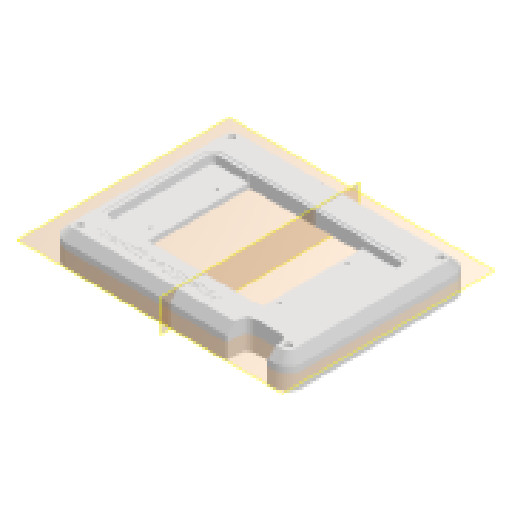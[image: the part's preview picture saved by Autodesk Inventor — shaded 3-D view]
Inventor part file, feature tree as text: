
AUTODESK INVENTOR PART (.ipt)
format: ipt  version: 2024.1 (Build 281209000, 209)  size: 909,824 bytes
history: native  units: mm
features: sketch x9, extrude x8, reference x8, projected_geometry x8, plane x5, other x4, chamfer x1, hole x1
ambient origin geometry x8: Origin, YZ Plane, XZ Plane, XY Plane, X Axis, Y Axis, Z Axis, Center Point
bodies: Volumenkörper1 (feature_tree)
feature tree (44):
  plane  "Arbeitsebene1"
  plane  "Arbeitsebene2"
  extrude  "Extrusion1"  Depth=10.0mm
  plane  "Arbeitsebene3"
  extrude  "Extrusion2"  Depth=10.0mm TaperAngle=0.0deg
  sketch  "Skizze3"  dims[d10=10.0mm d11=0.0mm d12=8.0mm d13=2.0mm d14=45.0deg]
  plane  "Arbeitsebene4"
  extrude  "Extrusion3"  Depth=8.0mm TaperAngle=45.0deg
  chamfer  "Fasen1"  [1 undecoded]
  extrude  "Extrusion4"  Depth=15.0mm TaperAngle=0.0deg
  extrude  "Extrusion5"  Depth=14.0mm
  extrude  "Extrusion6"  Depth=14.0mm
  hole  "Bohrung1"  [1 undecoded]
  extrude  "Extrusion7"  Depth=14.0mm
  extrude  "Extrusion8"  Depth=14.0mm
  plane  "Arbeitsebene5"
  sketch  "Skizze1"  dims[d2=1.0mm d3=0.0mm d4=10.0mm]
  reference  "Referenz2"
  reference  "Referenz3"
  reference  "Referenz4"
  reference  "Referenz5"
  reference  "Referenz6"
  sketch  "Skizze2"  dims[d5=5.0mm d7=10.0mm d8=0.0mm]
  sketch  "Skizze4"  dims[d15=40.0mm]
  reference  "Referenz9"
  projected_geometry  "Projizierte Kontur3"
  sketch  "Skizze5"  dims[d16=20.0mm]
  projected_geometry  "Projizierte Kontur4"
  sketch  "Skizze6"  dims[d17=7.0mm]
  projected_geometry  "Projizierte Kontur5"
  sketch  "Skizze7"  dims[d18=20.0mm d19=0.0mm d20=0.0mm]
  reference  "Referenz10"
  projected_geometry  "Projizierte Kontur6"
  sketch  "Skizze8"  dims[d21=6.0mm d22=15.0mm d23=0.0mm]
  projected_geometry  "Projizierte Kontur7"
  projected_geometry  "Projizierte Kontur8"
  sketch  "Skizze9"  dims[d24=0.5mm d25=0.0mm d26=3.3mm d27=6.0mm d28=6.5mm d29=3.5mm d30=90.0deg d31=15.0mm d32=20.594885mm d33=14.0mm d34=14.0mm d35=14.0mm d36=14.0mm d37=14.0mm d38=14.0mm d39=14.0mm d40=14.0mm d41=0.5mm d42=0.0mm d43=5.0mm d44=135.0deg d45=135.0deg d46=45.0mm d47=45.0deg d48=45.0deg d49=5.0mm d50=45.0deg d51=5.0mm d52=5.0mm d53=135.0deg d54=5.0mm d56=5.0mm d57=5.0mm d58=5.0mm d59=6.5mm d62=6.5mm d63=6.5mm d64=5.0mm d65=5.0mm d66=6.5mm d67=6.5mm d68=10.0mm d69=-3.490659mm d70=1.0mm d71=1.0mm d72=1.0mm d73=1.0mm d74=3.0mm d75=3.0mm d76=3.0mm d77=0.5mm]
  reference  "Referenz11"
  projected_geometry  "Projizierte Kontur9"
  projected_geometry  "Projizierte Kontur10"
  other  "Assembly_Planktoscope_Lid_Screen.iam"
  other  "00_raspberry pi display:1"
  other  "00_OutdoorCase_Type2000_toplid:1"
  other  "Baugruppe2"
note: 2 required parameter values undecoded (feature->parameter linkage not recoverable at this tier; creation-order binding heuristic only, values carry confidence <= 0.55)
